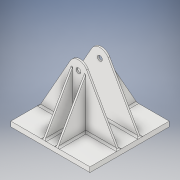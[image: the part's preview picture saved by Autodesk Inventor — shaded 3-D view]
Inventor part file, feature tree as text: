
AUTODESK INVENTOR PART (.ipt)
format: ipt  version: 2018 (Build 220112000, 112)  size: 254,464 bytes
history: native  units: in
note: dims shown in document units (in); Inventor stores cm internally (conversion verified against a paired STEP export)
features: extrude x4, sketch x4, fillet x2, plane x1, hole x1, projected_geometry x1
ambient origin geometry x8: Origin, YZ Plane, XZ Plane, XY Plane, X Axis, Y Axis, Z Axis, Center Point
bodies: Solid1 (feature_tree)
feature tree (13):
  extrude  "Extrusion1"  Depth=48.0in
  plane  "Work Plane1"
  extrude  "Extrusion2"  Depth=3.0in
  hole  "Hole1"  [1 undecoded]
  extrude  "Extrusion4"  Depth=1.0in
  extrude  "Extrusion6"  Depth=7.0in
  fillet  "Fillet1"  Radius=1.0in
  fillet  "Fillet2"  Radius=3.5in
  sketch  "Sketch1"  dims[d0=48.0in d1=48.0in]
  sketch  "Sketch2"  dims[d2=3.0in d3=0.0in d4=0.5in]
  sketch  "Sketch4"  dims[d5=0.5in d6=30.0in]
  projected_geometry  "Projected Loop1"
  sketch  "Sketch5"  dims[d7=14.0in d8=0.0in d14=1.0in d15=1.0in d16=3.0in d17=0.75in d18=0.375in d19=0.25in d20=0.5635in d21=1.0in d22=0.8108in d23=7.0in d24=1.0in d25=3.5in d26=14.0in d27=0.0in d28=1.0in d29=1.0in d32=14.0in d33=0.0in d34=1.0in d35=1.0in]
note: 1 required parameter value undecoded (feature->parameter linkage not recoverable at this tier; creation-order binding heuristic only, values carry confidence <= 0.55)
